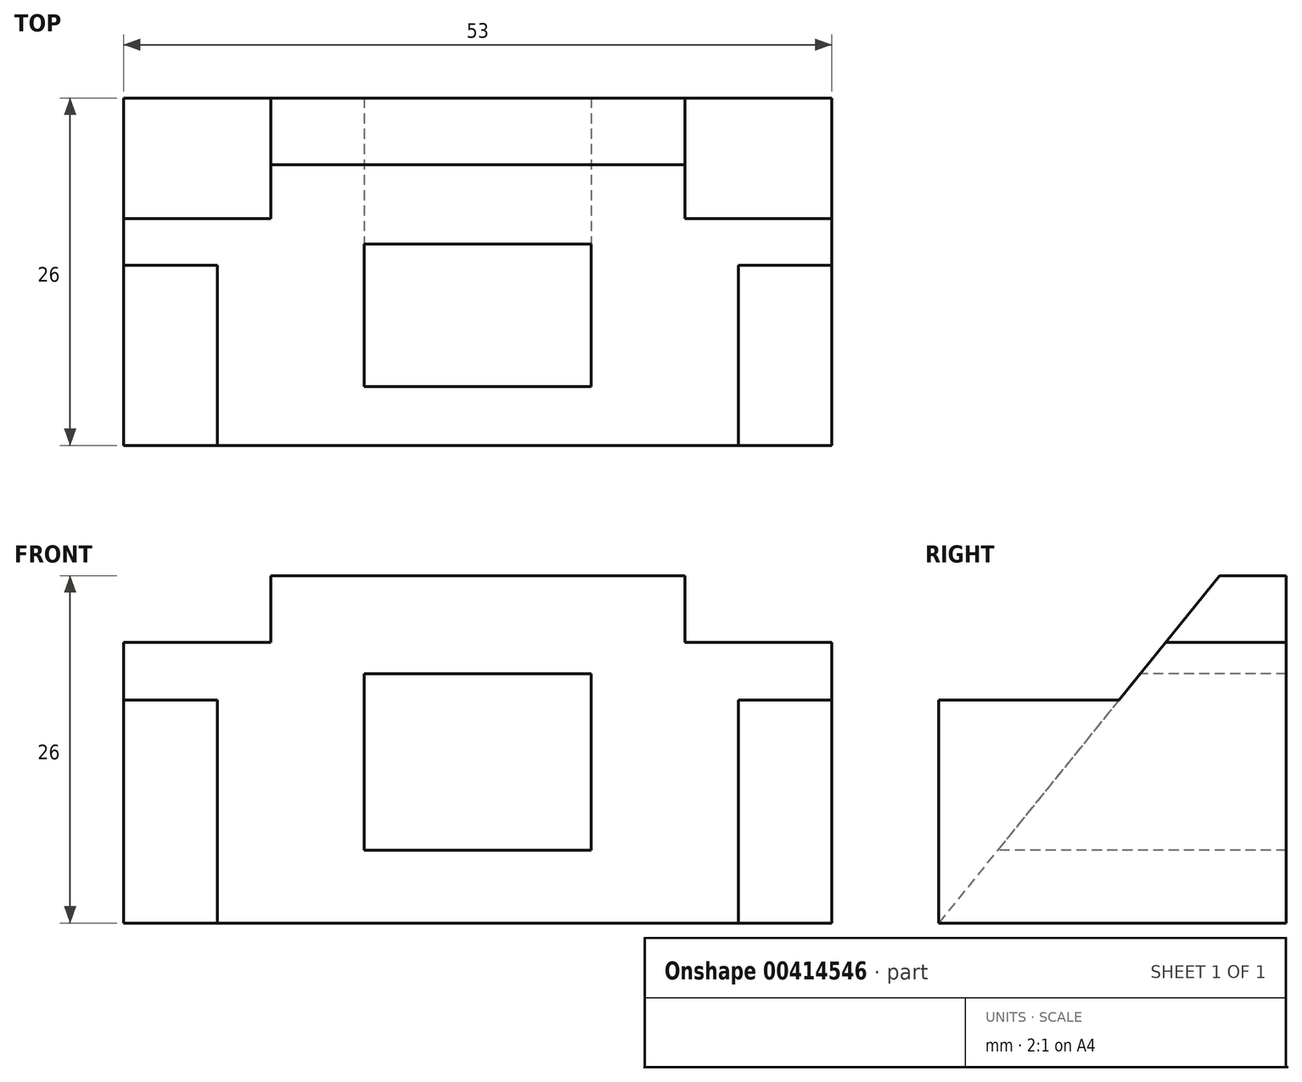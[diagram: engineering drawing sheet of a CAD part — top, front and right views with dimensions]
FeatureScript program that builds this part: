
annotation { "Feature Type Name" : "Feature", "Feature Type Description" : "" }
export const myFeature = defineFeature(function(context is Context, id is Id, definition is map)
    precondition{}
    {
        {
            var Q0;
            Q0=qCreatedBy(makeId("Front.planeOp"),FACE);
            var sketch = newSketch(context, id + "F0", { "sketchPlane" : qUnion([Q0])});
            skLineSegment(sketch, "E0.bottom", {"start": v(26.5, 13) * mm, "end": v(-26.5, 13) * mm});
            skLineSegment(sketch, "E0.top", {"start": v(26.5, -13) * mm, "end": v(-26.5, -13) * mm});
            skLineSegment(sketch, "E0.left", {"start": v(26.5, 13) * mm, "end": v(26.5, -13) * mm});
            skLineSegment(sketch, "E0.right", {"start": v(-26.5, 13) * mm, "end": v(-26.5, -13) * mm});
            skPoint(sketch, "E0.middle", {"position": v(0, 0) * mm});
            skSolve(sketch);
        }
        {
            var Q0;
            Q0 = qSketchRegion(id + "F0", true);
            extrude(context, id + "F1", {"entities" : qUnion([Q0]), "depth" : 26 * mm});
        }
        {
            var Q0;
            Q0=makeQuery(id+"F1.opExtrude","SWEPT_FACE",FACE,{"disambiguationData":[OSD([sQuery(id+"F0.wireOp",EDGE,"E0.left")])]});
            var sketch = newSketch(context, id + "F2", { "sketchPlane" : qUnion([Q0])});
            skLineSegment(sketch, "E1", {"start": v(0, 13) * mm, "end": v(-5, 13) * mm});
            skLineSegment(sketch, "E2", {"start": v(-5, 13) * mm, "end": v(-26, -13) * mm});
            skLineSegment(sketch, "E3", {"start": v(-5, 13) * mm, "end": v(-26, 13) * mm});
            skLineSegment(sketch, "E4", {"start": v(-26, 13) * mm, "end": v(-26, -13) * mm});
            skSolve(sketch);
        }
        {
            var Q0;
            Q0=makeQuery(id+"F2.imprint","IMPRINT",FACE,{"disambiguationData":[TD([[makeQuery(id+"F2.imprint","IMPRINT",EDGE,{"derivedFrom":sQuery(id+"F2.wireOp",EDGE,"E2")}),-1.0]])]});
            extrude(context, id + "F3", {"entities" : qUnion([Q0]), "operationType" : NewBodyOperationType.REMOVE, "oppositeDirection" : true, "depth" : 202.1 * mm});
        }
        {
            var Q0;
            Q0=makeQuery(id+"F1.opExtrude","CAP_FACE",FACE,{"disambiguationData":[OSD([sQuery(id+"F0.wireOp",EDGE,"E0.bottom"),sQuery(id+"F0.wireOp",EDGE,"E0.top"),sQuery(id+"F0.wireOp",EDGE,"E0.left"),sQuery(id+"F0.wireOp",EDGE,"E0.right")])],"isStart":true});
            var sketch = newSketch(context, id + "F4", { "sketchPlane" : qUnion([Q0])});
            skLineSegment(sketch, "E5.bottom", {"start": v(-26.5, -13) * mm, "end": v(-19.5, -13) * mm});
            skLineSegment(sketch, "E5.top", {"start": v(-26.5, 3.7) * mm, "end": v(-19.5, 3.7) * mm});
            skLineSegment(sketch, "E5.left", {"start": v(-26.5, -13) * mm, "end": v(-26.5, 3.7) * mm});
            skLineSegment(sketch, "E5.right", {"start": v(-19.5, -13) * mm, "end": v(-19.5, 3.7) * mm});
            skLineSegment(sketch, "E6.bottom", {"start": v(26.5, -13) * mm, "end": v(19.5, -13) * mm});
            skLineSegment(sketch, "E6.top", {"start": v(26.5, 3.7) * mm, "end": v(19.5, 3.7) * mm});
            skLineSegment(sketch, "E6.left", {"start": v(26.5, -13) * mm, "end": v(26.5, 3.7) * mm});
            skLineSegment(sketch, "E6.right", {"start": v(19.5, -13) * mm, "end": v(19.5, 3.7) * mm});
            skSolve(sketch);
        }
        {
            var Q0;
            Q0 = qSketchRegion(id + "F4", true);
            extrude(context, id + "F5", {"entities" : qUnion([Q0]), "operationType" : NewBodyOperationType.ADD, "oppositeDirection" : true, "depth" : 26 * mm});
        }
        {
            var Q0;
            Q0=makeQuery(id+"F1.opExtrude","CAP_FACE",FACE,{"disambiguationData":[OSD([sQuery(id+"F0.wireOp",EDGE,"E0.bottom"),sQuery(id+"F0.wireOp",EDGE,"E0.top"),sQuery(id+"F0.wireOp",EDGE,"E0.left"),sQuery(id+"F0.wireOp",EDGE,"E0.right")])],"isStart":true});
            var sketch = newSketch(context, id + "F6", { "sketchPlane" : qUnion([Q0])});
            skLineSegment(sketch, "E7.bottom", {"start": v(-26.5, 13) * mm, "end": v(-15.5, 13) * mm});
            skLineSegment(sketch, "E7.top", {"start": v(-26.5, 8) * mm, "end": v(-15.5, 8) * mm});
            skLineSegment(sketch, "E7.left", {"start": v(-26.5, 13) * mm, "end": v(-26.5, 8) * mm});
            skLineSegment(sketch, "E7.right", {"start": v(-15.5, 13) * mm, "end": v(-15.5, 8) * mm});
            skLineSegment(sketch, "E8.bottom", {"start": v(26.5, 13) * mm, "end": v(15.5, 13) * mm});
            skLineSegment(sketch, "E8.top", {"start": v(26.5, 8) * mm, "end": v(15.5, 8) * mm});
            skLineSegment(sketch, "E8.left", {"start": v(26.5, 13) * mm, "end": v(26.5, 8) * mm});
            skLineSegment(sketch, "E8.right", {"start": v(15.5, 13) * mm, "end": v(15.5, 8) * mm});
            skSolve(sketch);
        }
        {
            var Q0;
            Q0=makeQuery(id+"F6.imprint","IMPRINT",FACE,{"disambiguationData":[TD([[makeQuery(id+"F6.imprint","IMPRINT",EDGE,{"derivedFrom":sQuery(id+"F6.wireOp",EDGE,"E7.bottom")}),-1.0]])]});
            var Q1;
            Q1=makeQuery(id+"F6.imprint","IMPRINT",FACE,{"disambiguationData":[TD([[makeQuery(id+"F6.imprint","IMPRINT",EDGE,{"derivedFrom":sQuery(id+"F6.wireOp",EDGE,"E8.bottom")}),-1.0]])]});
            extrude(context, id + "F7", {"entities" : qUnion([Q0, Q1]), "operationType" : NewBodyOperationType.REMOVE, "oppositeDirection" : true, "depth" : 25 * mm});
        }
        {
            var Q0;
            Q0=makeQuery(id+"F3.boolean.opBoolean","COPY",FACE,{"derivedFrom":makeQuery(id+"F3.opExtrude","SWEPT_FACE",FACE,{"disambiguationData":[OSD([sQuery(id+"F2.wireOp",EDGE,"E2")])]})});
            var sketch = newSketch(context, id + "F8", { "sketchPlane" : qUnion([Q0])});
            skLineSegment(sketch, "E9.bottom", {"start": v(8.5, -2.45) * mm, "end": v(-8.5, -2.45) * mm});
            skLineSegment(sketch, "E9.top", {"start": v(8.5, -19.45) * mm, "end": v(-8.5, -19.45) * mm});
            skLineSegment(sketch, "E9.left", {"start": v(8.5, -2.45) * mm, "end": v(8.5, -19.45) * mm});
            skLineSegment(sketch, "E9.right", {"start": v(-8.5, -2.45) * mm, "end": v(-8.5, -19.45) * mm});
            skSolve(sketch);
        }
        {
            var Q0;
            Q0=makeQuery(id+"F1.opExtrude","CAP_FACE",FACE,{"disambiguationData":[OSD([sQuery(id+"F0.wireOp",EDGE,"E0.bottom"),sQuery(id+"F0.wireOp",EDGE,"E0.top"),sQuery(id+"F0.wireOp",EDGE,"E0.left"),sQuery(id+"F0.wireOp",EDGE,"E0.right")])],"isStart":true});
            var sketch = newSketch(context, id + "F9", { "sketchPlane" : qUnion([Q0])});
            skLineSegment(sketch, "E10.0", {"start": v(-8.5, 5.67) * mm, "end": v(8.5, 5.67) * mm});
            skLineSegment(sketch, "E11.0", {"start": v(-8.5, 5.67) * mm, "end": v(-8.5, -7.55) * mm});
            skLineSegment(sketch, "E12.0", {"start": v(8.5, 5.67) * mm, "end": v(8.5, -7.55) * mm});
            skLineSegment(sketch, "E13.0", {"start": v(-8.5, -7.55) * mm, "end": v(8.5, -7.55) * mm});
            skSolve(sketch);
        }
        {
            var Q1;
            Q1=makeQuery(id+"F9.imprint","IMPRINT",FACE,{"disambiguationData":[TD([[makeQuery(id+"F9.imprint","IMPRINT",EDGE,{"derivedFrom":sQuery(id+"F9.wireOp",EDGE,"E10.0")}),-1.0]])]});
            var Q2;
            Q2=makeQuery(id+"F8.imprint","IMPRINT",FACE,{"disambiguationData":[TD([[makeQuery(id+"F8.imprint","IMPRINT",EDGE,{"derivedFrom":sQuery(id+"F8.wireOp",EDGE,"E9.bottom")}),1.0]])]});
            loft(context, id + "F10", {"operationType" : NewBodyOperationType.REMOVE, "sheetProfilesArray" : [{ "sheetProfileEntities" : qUnion([Q1]) }, { "sheetProfileEntities" : qUnion([Q2]) }]});
        }
    });
